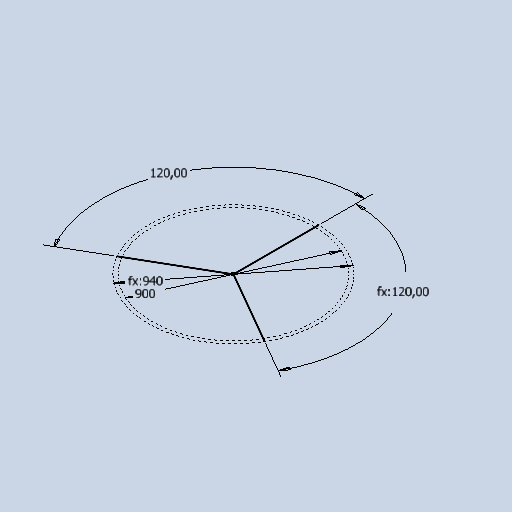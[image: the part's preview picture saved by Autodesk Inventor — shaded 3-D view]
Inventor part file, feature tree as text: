
AUTODESK INVENTOR PART (.ipt)
format: ipt  version: 2025.1 (Build 291241020, 241B)  size: 76,288 bytes
history: native  units: mm
features: sketch x1
ambient origin geometry x8: Origin, YZ Plane, XZ Plane, XY Plane, X Axis, Y Axis, Z Axis, Center Point
feature tree (1):
  sketch  "Sketch1"  dims[d1=900.0mm d2=120.0deg d3=120.0deg d4=940.0mm]
